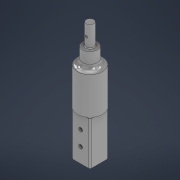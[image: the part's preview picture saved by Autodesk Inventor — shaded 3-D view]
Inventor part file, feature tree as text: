
AUTODESK INVENTOR PART (.ipt)
format: ipt  version: 2021 (Build 250183000, 183)  size: 266,752 bytes
history: native  units: mm
features: sketch x7, extrude x4, fillet x4, plane x2, hole x2
ambient origin geometry x8: Origin, YZ Plane, XZ Plane, XY Plane, X Axis, Y Axis, Z Axis, Center Point
bodies: Solid1 (feature_tree)
feature tree (19):
  extrude  "Extrusion1"  Depth=25.0mm
  fillet  "Fillet1"  Radius=12.5mm
  extrude  "Extrusion2"  Depth=2.5mm
  sketch  "Sketch3"  dims[d5=60.0mm d6=0.0mm d7=2.0mm]
  extrude  "Extrusion3"  Depth=2.0mm
  plane  "Work Plane1"
  hole  "Hole1"  [1 undecoded]
  plane  "Work Plane2"
  extrude  "Extrusion4"  Depth=10.0mm TaperAngle=0.0deg
  fillet  "Fillet3"  Radius=12.5mm
  fillet  "Fillet4"  Radius=15.0mm
  hole  "Hole2"  [1 undecoded]
  fillet  "Fillet5"  Radius=10.0mm
  sketch  "Sketch1"  dims[d0=25.0mm d1=25.0mm d2=12.5mm]
  sketch  "Sketch2"  dims[d3=12.5mm d4=2.5mm]
  sketch  "Sketch4"  dims[d8=33.941125mm d9=50.0mm d10=0.0mm]
  sketch  "Sketch5"  dims[d11=10.0mm d12=50.0mm d13=0.0mm d19=12.5mm]
  sketch  "Sketch6"  dims[d20=3.242mm d21=8.0mm d22=4.0mm d23=2.0mm d24=90.0deg d25=8.0mm d26=0.0mm d28=15.0mm]
  sketch  "Sketch7"  dims[d29=-28.0mm d30=5.0mm d31=10.0mm d32=0.0mm d33=1.0mm d34=7.0mm d35=0.0mm d36=0.0mm d37=20.0mm d38=20.0mm d39=5.0mm d40=6.0mm d41=4.0mm d42=2.0mm d43=90.0deg d44=8.0mm d45=20.594885mm d46=2.0mm]
note: 2 required parameter values undecoded (feature->parameter linkage not recoverable at this tier; creation-order binding heuristic only, values carry confidence <= 0.55)
